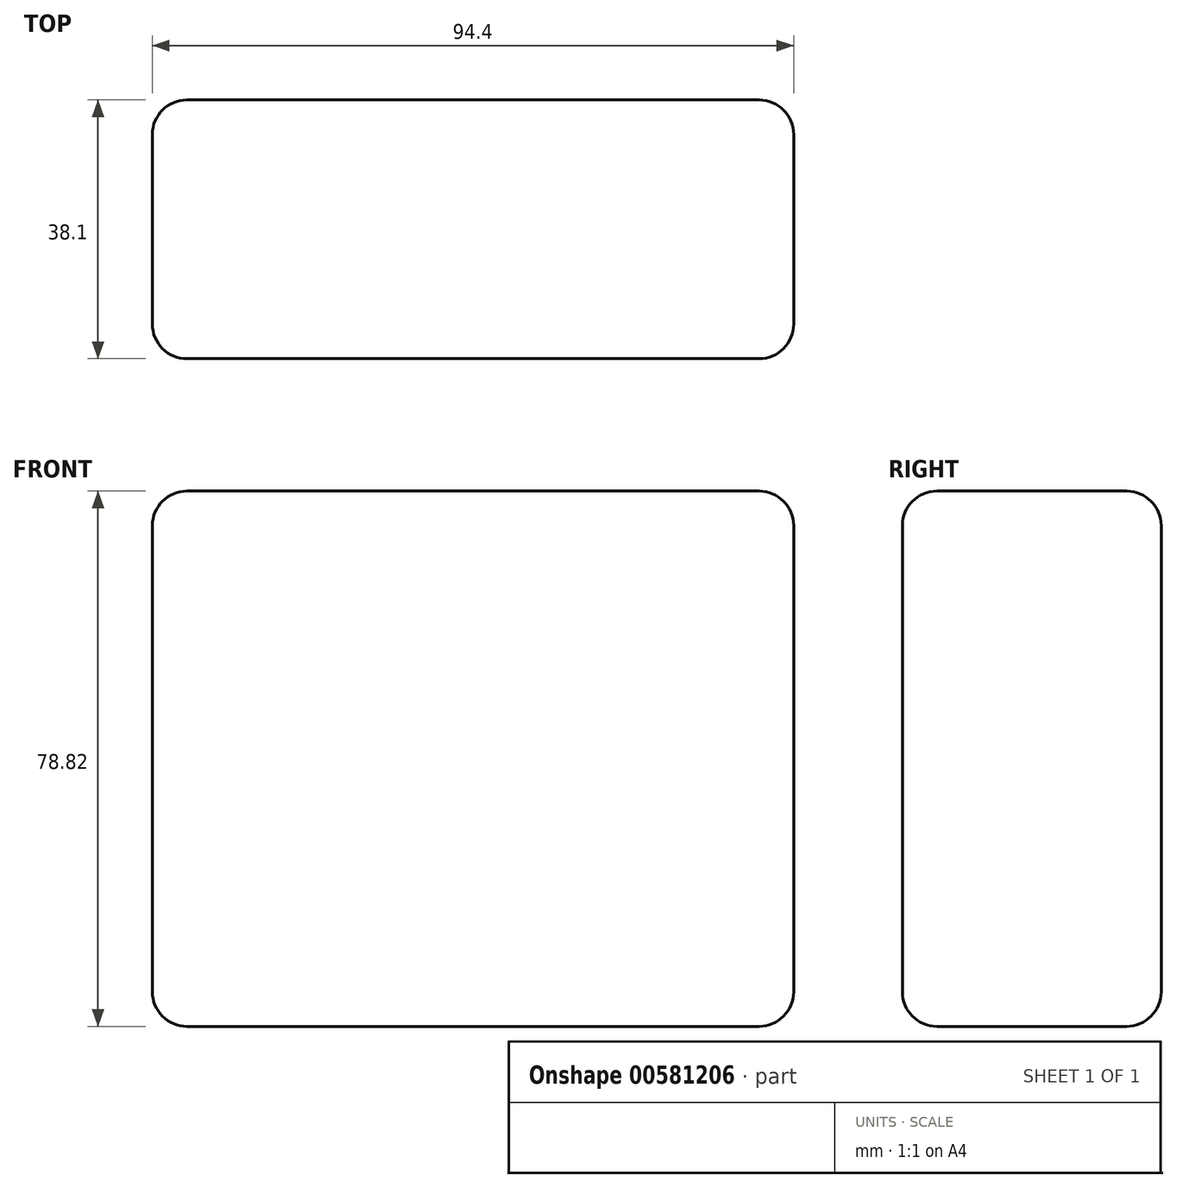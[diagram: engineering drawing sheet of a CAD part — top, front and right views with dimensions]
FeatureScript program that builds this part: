
annotation { "Feature Type Name" : "Feature", "Feature Type Description" : "" }
export const myFeature = defineFeature(function(context is Context, id is Id, definition is map)
    precondition{}
    {
        {
            var Q0;
            Q0=qCreatedBy(makeId("Front.planeOp"),FACE);
            var sketch = newSketch(context, id + "F0", { "sketchPlane" : qUnion([Q0])});
            skLineSegment(sketch, "E0.bottom", {"start": v(47.2, 39.4) * mm, "end": v(-47.2, 39.4) * mm});
            skLineSegment(sketch, "E0.top", {"start": v(47.2, -39.4) * mm, "end": v(-47.2, -39.4) * mm});
            skLineSegment(sketch, "E0.left", {"start": v(47.2, 39.4) * mm, "end": v(47.2, -39.4) * mm});
            skLineSegment(sketch, "E0.right", {"start": v(-47.2, 39.4) * mm, "end": v(-47.2, -39.4) * mm});
            skPoint(sketch, "E0.middle", {"position": v(0, 0) * mm});
            skSolve(sketch);
        }
        {
            var Q0;
            Q0=makeQuery(id+"F0.imprint","IMPRINT",FACE,{"disambiguationData":[TD([[makeQuery(id+"F0.imprint","IMPRINT",EDGE,{"derivedFrom":sQuery(id+"F0.wireOp",EDGE,"E0.bottom")}),1.0]])]});
            var Q1;
            Q1 = qSketchRegion(id + "F0", true);
            extrude(context, id + "F1", {"entities" : qUnion([Q0, Q1]), "depth" : 38.1 * mm, "offsetDistance" : 25.4 * mm});
        }
        {
            var Q0;
            Q0=makeQuery(id+"F1.opExtrude","CAP_FACE",FACE,{"disambiguationData":[OSD([sQuery(id+"F0.wireOp",EDGE,"E0.bottom"),sQuery(id+"F0.wireOp",EDGE,"E0.top"),sQuery(id+"F0.wireOp",EDGE,"E0.left"),sQuery(id+"F0.wireOp",EDGE,"E0.right")])],"isStart":false});
            fillet(context, id + "F2", {"entities" : qUnion([Q0]), "radius" : 5.08 * mm, "tangentPropagation" : true, "allowEdgeOverflow" : false});
        }
        {
            var Q0;
            Q0=makeQuery(id+"F1.opExtrude","CAP_FACE",FACE,{"disambiguationData":[OSD([sQuery(id+"F0.wireOp",EDGE,"E0.bottom"),sQuery(id+"F0.wireOp",EDGE,"E0.top"),sQuery(id+"F0.wireOp",EDGE,"E0.left"),sQuery(id+"F0.wireOp",EDGE,"E0.right")])],"isStart":true});
            fillet(context, id + "F3", {"entities" : qUnion([Q0]), "radius" : 5.08 * mm, "tangentPropagation" : true, "allowEdgeOverflow" : false});
        }
        {
            var Q0;
            Q0=makeQuery(id+"F1.opExtrude","SWEPT_FACE",FACE,{"disambiguationData":[OSD([sQuery(id+"F0.wireOp",EDGE,"E0.bottom")])]});
            fillet(context, id + "F4", {"entities" : qUnion([Q0]), "radius" : 5.08 * mm, "tangentPropagation" : true, "allowEdgeOverflow" : false});
        }
        {
            var Q0;
            Q0=makeQuery(id+"F1.opExtrude","SWEPT_FACE",FACE,{"disambiguationData":[OSD([sQuery(id+"F0.wireOp",EDGE,"E0.right")])]});
            fillet(context, id + "F5", {"entities" : qUnion([Q0]), "radius" : 5.08 * mm, "tangentPropagation" : true, "allowEdgeOverflow" : false});
        }
        {
            var Q0;
            Q0=makeQuery(id+"F1.opExtrude","SWEPT_FACE",FACE,{"disambiguationData":[OSD([sQuery(id+"F0.wireOp",EDGE,"E0.top")])]});
            fillet(context, id + "F6", {"entities" : qUnion([Q0]), "radius" : 5.08 * mm, "tangentPropagation" : true, "allowEdgeOverflow" : false});
        }
    });
